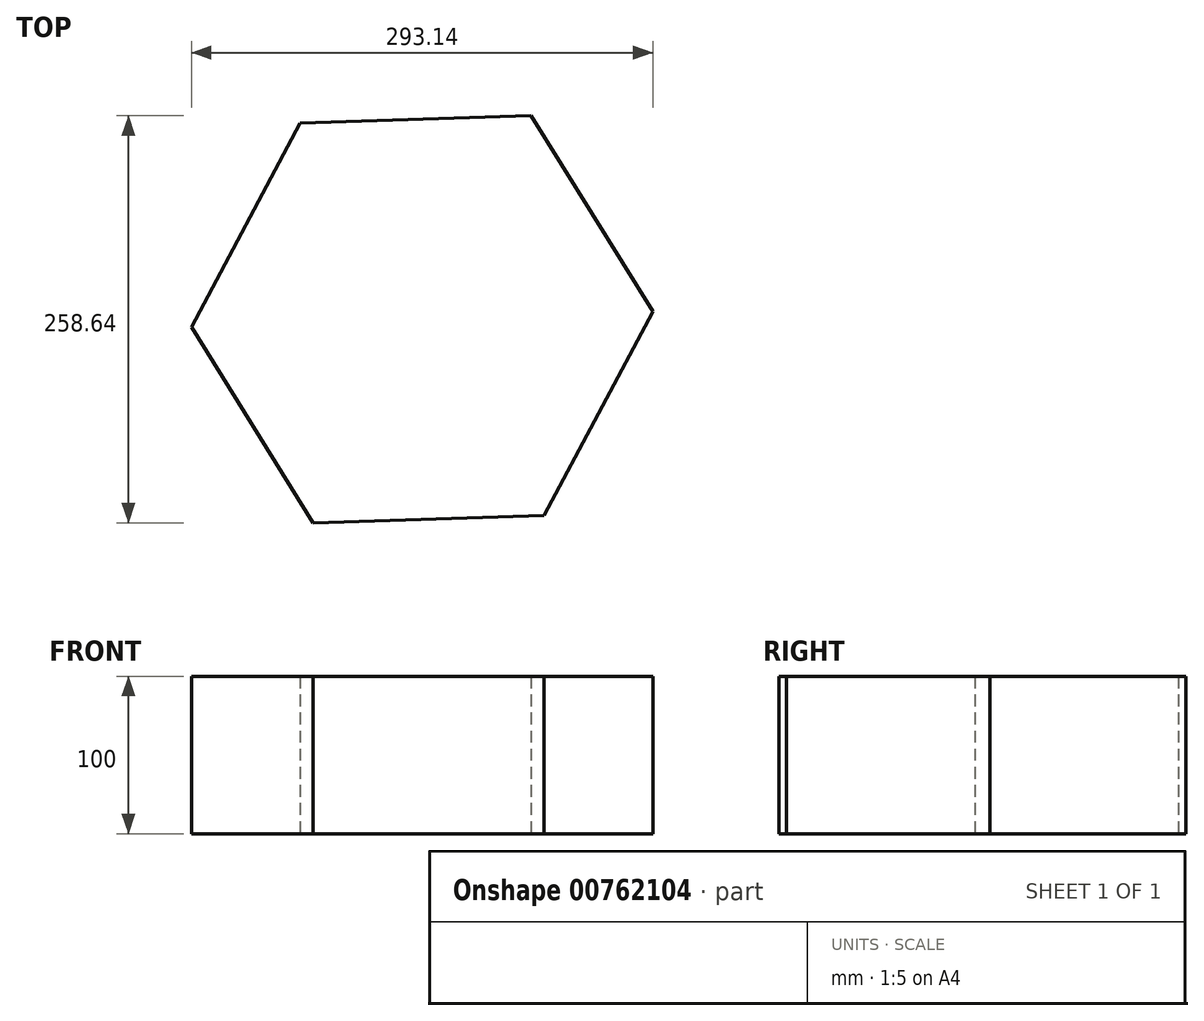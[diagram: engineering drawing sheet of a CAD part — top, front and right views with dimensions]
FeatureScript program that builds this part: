
annotation { "Feature Type Name" : "Feature", "Feature Type Description" : "" }
export const myFeature = defineFeature(function(context is Context, id is Id, definition is map)
    precondition{}
    {
        {
            var Q0;
            Q0=qCreatedBy(makeId("Top.planeOp"),FACE);
            var sketch = newSketch(context, id + "F0", { "sketchPlane" : qUnion([Q0])});
            skCircle(sketch, "E0.cCircle", {"center": v(0, 0) * mm, "radius": 127 * mm, "construction": true});
            skLineSegment(sketch, "E0.0", {"start": v(69.15, 129.32) * mm, "end": v(146.57, 4.78) * mm});
            skLineSegment(sketch, "E0.1", {"start": v(146.57, 4.78) * mm, "end": v(77.42, -124.55) * mm});
            skLineSegment(sketch, "E0.2", {"start": v(77.42, -124.55) * mm, "end": v(-69.15, -129.32) * mm});
            skLineSegment(sketch, "E0.3", {"start": v(-69.15, -129.32) * mm, "end": v(-146.57, -4.78) * mm});
            skLineSegment(sketch, "E0.4", {"start": v(-146.57, -4.78) * mm, "end": v(-77.42, 124.55) * mm});
            skLineSegment(sketch, "E0.5", {"start": v(-77.42, 124.55) * mm, "end": v(69.15, 129.32) * mm});
            skPoint(sketch, "E0.0.midPoint", {"position": v(107.86, 67.05) * mm});
            skSolve(sketch);
        }
        {
            var Q0;
            Q0 = qSketchRegion(id + "F0", true);
            extrude(context, id + "F1", {"entities" : qUnion([Q0]), "depth" : 100 * mm, "offsetDistance" : 25 * mm});
        }
        {
            var Q0;
            Q0 = qSketchRegion(id + "F0", true);
            extrude(context, id + "F2", {"entities" : qUnion([Q0]), "operationType" : NewBodyOperationType.ADD, "depth" : 100 * mm, "offsetDistance" : 25 * mm});
        }
    });
